# Revit family: 304_F380_4__
name_source: partatom
category: Pipe Accessories
units: mm (PartAtom-declared; Revit-internal decimal feet)

## family parameters
Always vertical = Yes
Cut with Voids When Loaded = No
Part Type = Valve - Breaks Into
Round Connector Dimension = Use Diameter
Shared = No
Work Plane-Based = No

## types (3) — shared parameters
A = 60.00°
CenSd_RN_6 = 10 mm  [stored 0.0328084 ft]
Description = K - Automatic Balancing Valve - Accessible Pre-Set Cartridge
L2D_Min = 3048 mm  [stored 10 ft]
Manufacturer = FlowCon
QmdConnectorList = 301;D;302;D
R3 = 6 mm  [stored 0.019685 ft]
R4 = 11 mm  [stored 0.0360892 ft]
RN = 12 mm  [stored 0.0393701 ft]
URL = http://flowcon.com
magiPartTypeId = 304
magiProductFamilyId = F380.4.*
zero-valued in all types: MC_Default_elevation

## per-type parameters (varying)
| type | CenSd_SW_6 | D | H4 | H5 | H6 | L1 | L1__ve | L2 | L2D | L3 | L4 | LL | R | R1 | R2 | SW | W2D | magiProductId |
| F380.4.E.B | 11 mm  [stored 0.0360892 ft] | 15 mm | 29 mm | 43 mm | 31 mm | 14 mm  [stored 0.0459318 ft] | -14 mm | 61 mm | 89 mm | 31 mm | 25 mm  [stored 0.082021 ft] | 45 mm | 8 mm  [stored 0.0262467 ft] | 10 mm  [stored 0.0328084 ft] | 14 mm  [stored 0.0459318 ft] | 13 mm  [stored 0.0426509 ft] | 15 mm  [stored 0.0492126 ft] | F380.4.E |
| F380.4.H.B | 18 mm  [stored 0.0590551 ft] | 25 mm | 33 mm  [stored 0.108268 ft] | 49 mm | 33 mm  [stored 0.108268 ft] | 17 mm | -17 mm | 71 mm | 105 mm  [stored 0.344488 ft] | 37 mm | 28 mm | 53 mm | 13 mm  [stored 0.0426509 ft] | 16 mm | 23 mm | 20 mm  [stored 0.0656168 ft] | 25 mm  [stored 0.082021 ft] | F380.4.H |
| F380.4.F.B | 11 mm  [stored 0.0360892 ft] | 20 mm | 31 mm | 46 mm | 32 mm | 15 mm  [stored 0.0492126 ft] | -15 mm | 66 mm | 96 mm | 34 mm | 26 mm | 48 mm | 10 mm  [stored 0.0328084 ft] | 10 mm  [stored 0.0328084 ft] | 18 mm  [stored 0.0590551 ft] | 13 mm  [stored 0.0426509 ft] | 20 mm  [stored 0.0656168 ft] | F380.4.F |

note: column(s) folded — value = type name in every type: magiProductCode

note: [stored X ft] marks values corroborated as IEEE doubles in the binary element streams (Revit-internal decimal feet)

## geometry (parser evidence)
native form markers: Sweep x1
no freeform markers — native parametric forms only
